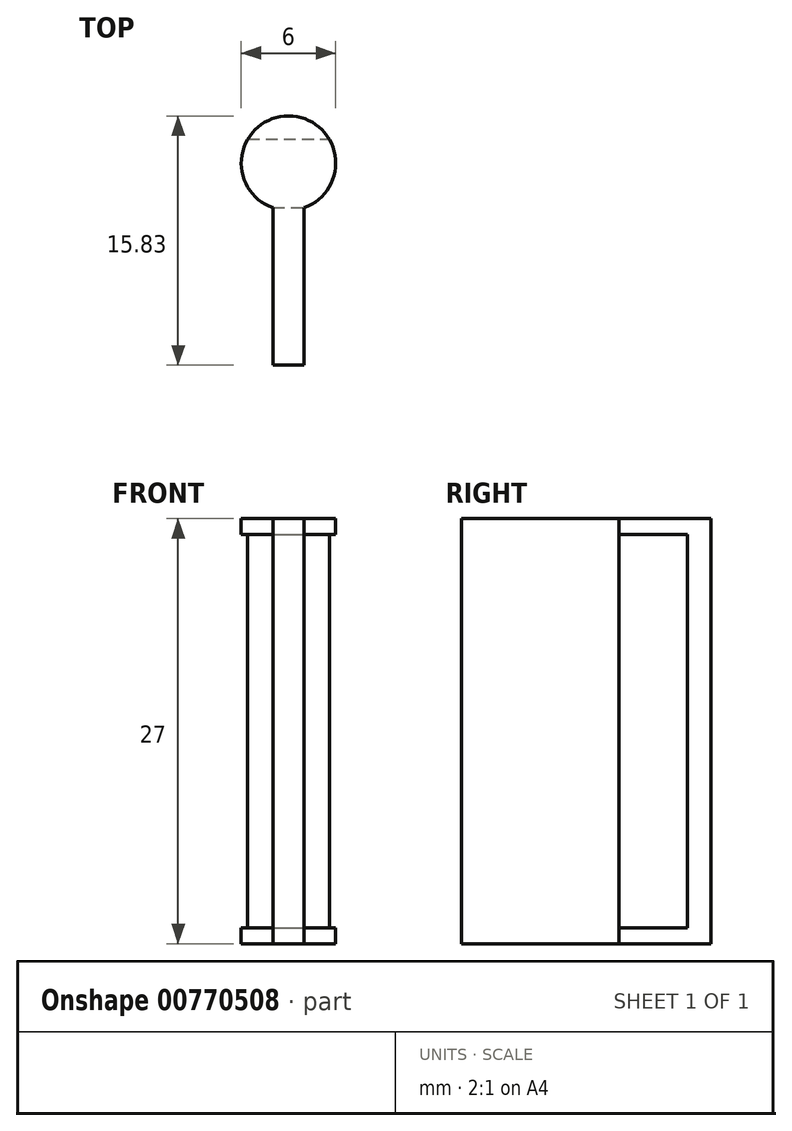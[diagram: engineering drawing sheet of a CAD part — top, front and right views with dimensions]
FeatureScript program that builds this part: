
annotation { "Feature Type Name" : "Feature", "Feature Type Description" : "" }
export const myFeature = defineFeature(function(context is Context, id is Id, definition is map)
    precondition{}
    {
        {
            var Q0;
            Q0=qCreatedBy(makeId("Top.planeOp"),FACE);
            var sketch = newSketch(context, id + "F0", { "sketchPlane" : qUnion([Q0])});
            skLineSegment(sketch, "E0.left", {"start": v(-9.83, 7.74) * mm, "end": v(-9.83, 17.74) * mm});
            skLineSegment(sketch, "E0.right", {"start": v(-7.83, 7.74) * mm, "end": v(-7.83, 17.74) * mm});
            skArc(sketch, "E1", {"start": v(-7.83, 17.74) * mm, "mid": v(-8.83, 23.57) * mm, "end": v(-9.83, 17.74) * mm});
            skLineSegment(sketch, "E2", {"start": v(-9.83, 7.74) * mm, "end": v(-7.83, 7.74) * mm});
            skPoint(sketch, "E3.center.orphan", {"position": v(-8.83, 0) * mm});
            skSolve(sketch);
        }
        {
            var Q0;
            Q0=makeQuery(id+"F0.imprint","IMPRINT",FACE,{"disambiguationData":[TD([[makeQuery(id+"F0.imprint","IMPRINT",EDGE,{"derivedFrom":sQuery(id+"F0.wireOp",EDGE,"E3")}),1.0]])]});
            var Q1;
            Q1=makeQuery(id+"F0.imprint","IMPRINT",FACE,{"disambiguationData":[TD([[makeQuery(id+"F0.imprint","IMPRINT",EDGE,{"derivedFrom":sQuery(id+"F0.wireOp",EDGE,"E0.left")}),-1.0]])]});
            extrude(context, id + "F1", {"entities" : qUnion([Q0, Q1]), "depth" : 27 * mm, "offsetDistance" : 25 * mm});
        }
        {
            var Q0;
            Q0=qCreatedBy(makeId("Right.planeOp"),FACE);
            var sketch = newSketch(context, id + "F2", { "sketchPlane" : qUnion([Q0])});
            skLineSegment(sketch, "E4.bottom", {"start": v(22.08, 26) * mm, "end": v(17.74, 26) * mm});
            skLineSegment(sketch, "E4.top", {"start": v(22.08, 1) * mm, "end": v(17.74, 1) * mm});
            skLineSegment(sketch, "E4.left", {"start": v(22.08, 26) * mm, "end": v(22.08, 1) * mm});
            skLineSegment(sketch, "E4.right", {"start": v(17.74, 26) * mm, "end": v(17.74, 1) * mm});
            skSolve(sketch);
        }
        {
            var Q0;
            Q0 = qSketchRegion(id + "F2", true);
            extrude(context, id + "F3", {"entities" : qUnion([Q0]), "operationType" : NewBodyOperationType.REMOVE, "oppositeDirection" : true, "depth" : 25 * mm, "offsetDistance" : 25 * mm});
        }
    });
